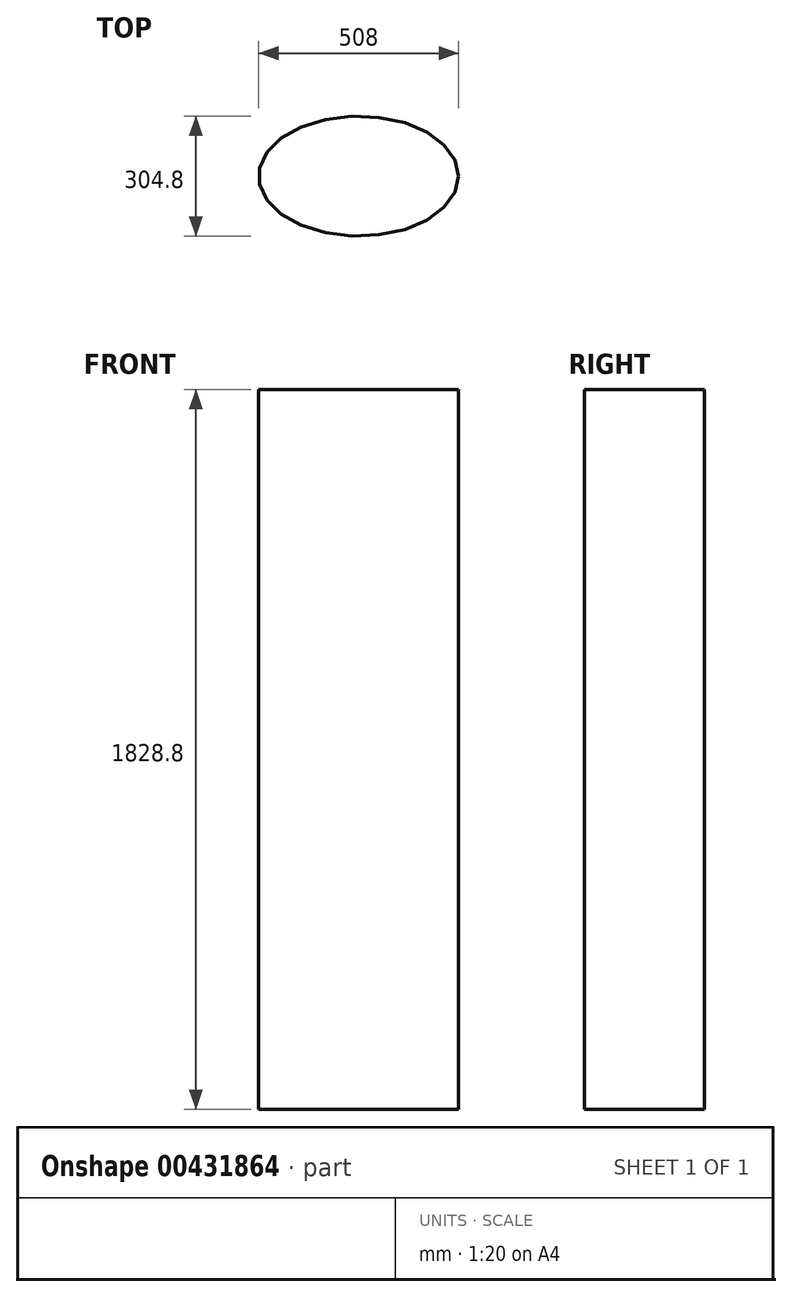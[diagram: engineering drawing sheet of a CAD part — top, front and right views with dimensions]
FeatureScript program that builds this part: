
annotation { "Feature Type Name" : "Feature", "Feature Type Description" : "" }
export const myFeature = defineFeature(function(context is Context, id is Id, definition is map)
    precondition{}
    {
        {
            var Q0;
            Q0=qCreatedBy(makeId("Top.planeOp"),FACE);
            var sketch = newSketch(context, id + "F0", { "sketchPlane" : qUnion([Q0])});
            skEllipse(sketch, "E0", {"center": v(0, 0) * mm, "majorRadius": 254 * mm, "minorRadius": 152.4 * mm, "majorAxis": v(1, 0)});
            skSolve(sketch);
        }
        {
            var Q0;
            Q0 = qSketchRegion(id + "F0", true);
            extrude(context, id + "F1", {"entities" : qUnion([Q0]), "depth" : 914.4 * mm, "hasSecondDirection" : true, "secondDirectionOppositeDirection" : true, "secondDirectionDepth" : 914.4 * mm});
        }
    });
